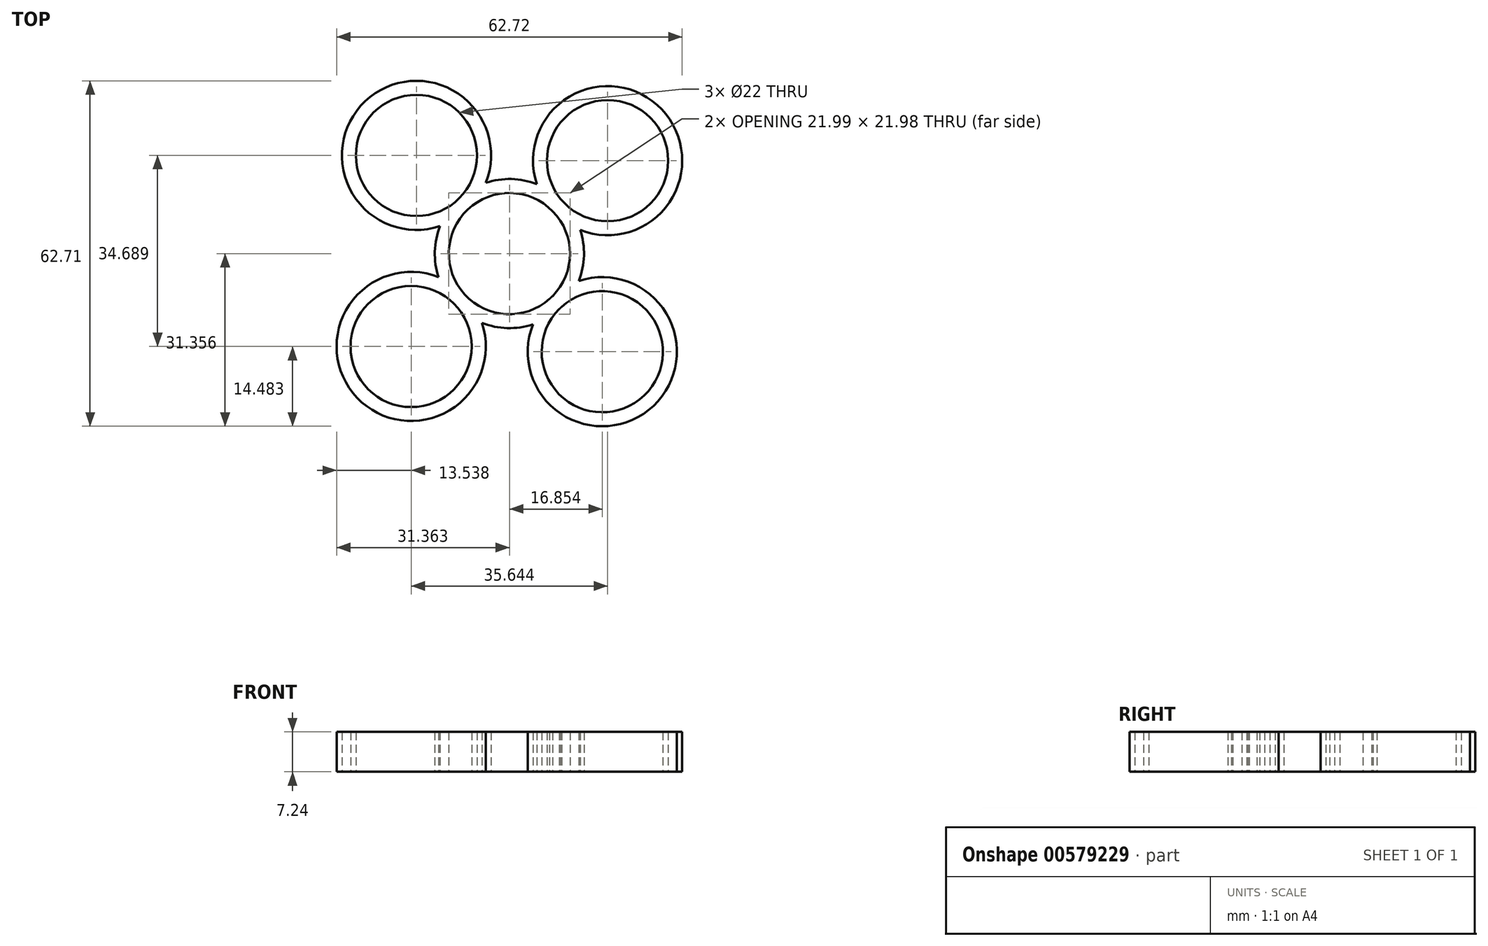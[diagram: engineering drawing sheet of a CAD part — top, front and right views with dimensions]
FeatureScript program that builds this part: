
annotation { "Feature Type Name" : "Feature", "Feature Type Description" : "" }
export const myFeature = defineFeature(function(context is Context, id is Id, definition is map)
    precondition{}
    {
        {
            var Q0;
            Q0=qCreatedBy(makeId("Top.planeOp"),FACE);
            var sketch = newSketch(context, id + "F0", { "sketchPlane" : qUnion([Q0])});
            skCircle(sketch, "E0", {"center": v(0, 0) * mm, "radius": 11 * mm});
            skArc(sketch, "E1", {"start": v(9.65, -9.5) * mm, "mid": v(-9.48, 9.67) * mm, "end": v(9.3, -9.83) * mm});
            skLineSegment(sketch, "E2", {"start": v(36.9, 34.92) * mm, "end": v(0, 0) * mm});
            skLineSegment(sketch, "E3", {"start": v(0, 0) * mm, "end": v(-36.9, -34.92) * mm});
            skLineSegment(sketch, "E4", {"start": v(-9.83, -9.3) * mm, "end": v(0, 0) * mm});
            skLineSegment(sketch, "E5", {"start": v(0, 0) * mm, "end": v(-34.92, 36.9) * mm});
            skLineSegment(sketch, "E6", {"start": v(-34.92, 36.9) * mm, "end": v(0, 0) * mm});
            skPoint(sketch, "E7.center.orphan", {"position": v(17.46, -18.45) * mm});
            skPoint(sketch, "E8.trimOffspring.end.orphan", {"position": v(34.92, -36.9) * mm});
            skLineSegment(sketch, "E9", {"start": v(0, 0) * mm, "end": v(34.92, -36.9) * mm});
            skArc(sketch, "E10", {"start": v(9.65, -9.5) * mm, "mid": v(9.48, -9.66) * mm, "end": v(9.3, -9.83) * mm});
            skPoint(sketch, "E10.first.point", {"position": v(9.3, -9.83) * mm});
            skPoint(sketch, "E10.second.point", {"position": v(21.33, -22.54) * mm});
            skPoint(sketch, "E10.third.point", {"position": v(24.34, -16.58) * mm});
            skSolve(sketch);
        }
        {
            var Q0;
            Q0=qCreatedBy(makeId("Top.planeOp"),FACE);
            var sketch = newSketch(context, id + "F1", { "sketchPlane" : qUnion([Q0])});
            skCircle(sketch, "E11", {"center": v(16.86, -17.81) * mm, "radius": 11 * mm});
            skPoint(sketch, "E11.first.point", {"position": v(9.24, -9.89) * mm});
            skPoint(sketch, "E11.second.point", {"position": v(24.4, -25.81) * mm});
            skPoint(sketch, "E11.third.point", {"position": v(9.67, -26.13) * mm});
            skCircle(sketch, "E12", {"center": v(16.86, -17.81) * mm, "radius": 13.54 * mm});
            skSolve(sketch);
        }
        {
            var Q0;
            Q0=qCreatedBy(makeId("Top.planeOp"),FACE);
            var sketch = newSketch(context, id + "F2", { "sketchPlane" : qUnion([Q0])});
            skCircle(sketch, "E13", {"center": v(-17.82, -16.87) * mm, "radius": 11 * mm});
            skPoint(sketch, "E13.first.point", {"position": v(-9.83, -9.3) * mm});
            skPoint(sketch, "E13.second.point", {"position": v(-25.5, -24.74) * mm});
            skPoint(sketch, "E13.third.point", {"position": v(-14.88, -27.47) * mm});
            skCircle(sketch, "E14", {"center": v(-17.82, -16.87) * mm, "radius": 13.54 * mm});
            skSolve(sketch);
        }
        {
            var Q0;
            Q0=qCreatedBy(makeId("Top.planeOp"),FACE);
            var sketch = newSketch(context, id + "F3", { "sketchPlane" : qUnion([Q0])});
            skCircle(sketch, "E15", {"center": v(-16.87, 17.82) * mm, "radius": 11 * mm});
            skPoint(sketch, "E15.first.point", {"position": v(-9.78, 9.41) * mm});
            skPoint(sketch, "E15.second.point", {"position": v(-24.72, 25.52) * mm});
            skPoint(sketch, "E15.third.point", {"position": v(-25.3, 10.76) * mm});
            skCircle(sketch, "E16", {"center": v(-16.87, 17.82) * mm, "radius": 13.54 * mm});
            skSolve(sketch);
        }
        {
            var Q0;
            Q0=qCreatedBy(makeId("Top.planeOp"),FACE);
            var sketch = newSketch(context, id + "F4", { "sketchPlane" : qUnion([Q0])});
            skCircle(sketch, "E17", {"center": v(17.82, 16.87) * mm, "radius": 11 * mm});
            skPoint(sketch, "E17.first.point", {"position": v(8.59, 10.9) * mm});
            skPoint(sketch, "E17.second.point", {"position": v(25, 25.2) * mm});
            skPoint(sketch, "E17.third.point", {"position": v(24.65, 8.25) * mm});
            skCircle(sketch, "E18", {"center": v(17.82, 16.87) * mm, "radius": 13.54 * mm});
            skSolve(sketch);
        }
        {
            var Q0;
            Q0 = qSketchRegion(id + "F0", true);
            extrude(context, id + "F5", {"entities" : qUnion([Q0]), "depth" : 7.24 * mm, "offsetDistance" : 25.4 * mm});
        }
        {
            var Q0;
            Q0 = qSketchRegion(id + "F1", true);
            extrude(context, id + "F6", {"entities" : qUnion([Q0]), "operationType" : NewBodyOperationType.ADD, "depth" : 7.24 * mm, "offsetDistance" : 25.4 * mm});
        }
        {
            var Q0;
            Q0 = qSketchRegion(id + "F2", true);
            extrude(context, id + "F7", {"entities" : qUnion([Q0]), "operationType" : NewBodyOperationType.ADD, "depth" : 7.24 * mm, "offsetDistance" : 25.4 * mm});
        }
        {
            var Q0;
            Q0 = qSketchRegion(id + "F3", true);
            extrude(context, id + "F8", {"entities" : qUnion([Q0]), "operationType" : NewBodyOperationType.ADD, "depth" : 7.24 * mm, "offsetDistance" : 25.4 * mm});
        }
        {
            var Q0;
            Q0 = qSketchRegion(id + "F4", true);
            extrude(context, id + "F9", {"entities" : qUnion([Q0]), "operationType" : NewBodyOperationType.ADD, "depth" : 7.24 * mm, "offsetDistance" : 25.4 * mm});
        }
    });
